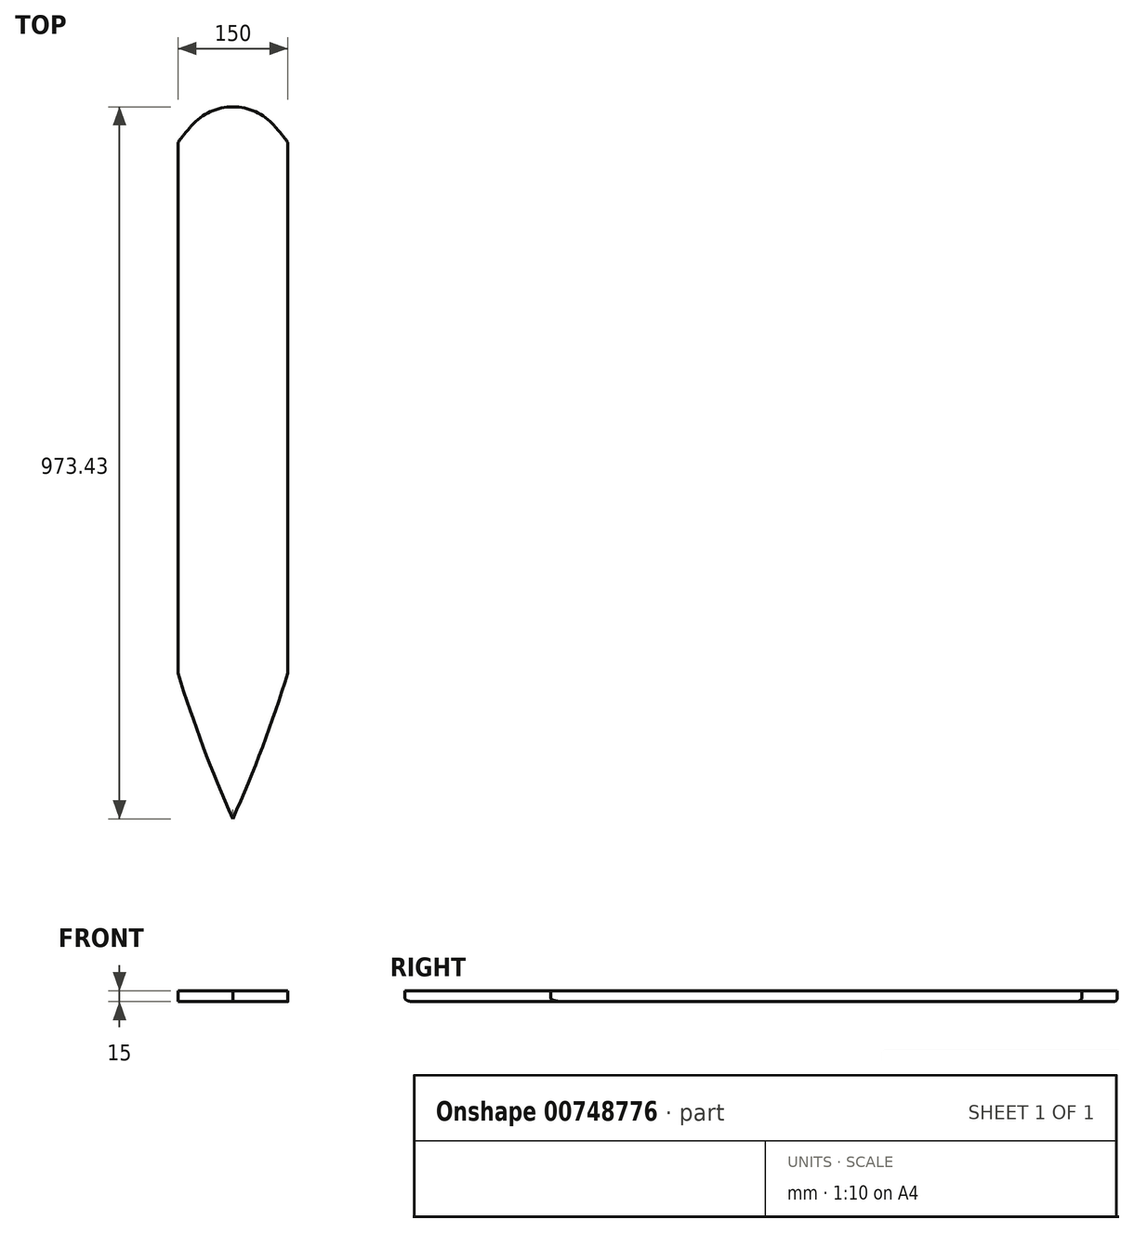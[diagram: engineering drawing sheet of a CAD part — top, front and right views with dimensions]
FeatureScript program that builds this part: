
annotation { "Feature Type Name" : "Feature", "Feature Type Description" : "" }
export const myFeature = defineFeature(function(context is Context, id is Id, definition is map)
    precondition{}
    {
        {
            var Q0;
            Q0=qCreatedBy(makeId("Top.planeOp"),FACE);
            var sketch = newSketch(context, id + "F0", { "sketchPlane" : qUnion([Q0])});
            skLineSegment(sketch, "E0.bottom", {"start": v(150, 500) * mm, "end": v(-150, 500) * mm, "construction": true});
            skLineSegment(sketch, "E0.top", {"start": v(150, -500) * mm, "end": v(-150, -500) * mm, "construction": true});
            skLineSegment(sketch, "E0.left", {"start": v(150, 500) * mm, "end": v(150, -500) * mm});
            skLineSegment(sketch, "E0.right", {"start": v(-150, 500) * mm, "end": v(-150, -500) * mm, "construction": true});
            skPoint(sketch, "E0.middle", {"position": v(0, 0) * mm});
            skLineSegment(sketch, "E1", {"start": v(0, 500) * mm, "end": v(0, -500) * mm, "construction": true});
            skPoint(sketch, "E2.orphan", {"position": v(0, 500) * mm});
            skArc(sketch, "E3", {"start": v(0, 500) * mm, "mid": v(-110.41, 367.7) * mm, "end": v(-150, 200) * mm});
            skArc(sketch, "E4.MirrorCS", {"start": v(150, 200) * mm, "mid": v(112.08, -157.95) * mm, "end": v(0, -500) * mm});
            skArc(sketch, "E5.MirrorCS", {"start": v(0, 500) * mm, "mid": v(110.41, 367.7) * mm, "end": v(150, 200) * mm});
            skArc(sketch, "E6.trimOffspring", {"start": v(-150, 200) * mm, "mid": v(-112.08, -157.95) * mm, "end": v(0, -500) * mm});
            skLineSegment(sketch, "E7", {"start": v(0, 200) * mm, "end": v(-1558.33, 200) * mm, "construction": true});
            skLineSegment(sketch, "E8", {"start": v(0, 200) * mm, "end": v(1558.33, 200) * mm, "construction": true});
            skLineSegment(sketch, "E9.bottom", {"start": v(75, -500) * mm, "end": v(-75, -500) * mm});
            skLineSegment(sketch, "E9.top", {"start": v(75, 500) * mm, "end": v(-75, 500) * mm});
            skLineSegment(sketch, "E9.left", {"start": v(75, -500) * mm, "end": v(75, 500) * mm});
            skLineSegment(sketch, "E9.right", {"start": v(-75, -500) * mm, "end": v(-75, 500) * mm});
            skLineSegment(sketch, "E10.bottom", {"start": v(0, 200) * mm, "end": v(0, 200) * mm});
            skLineSegment(sketch, "E10.top", {"start": v(0, 0) * mm, "end": v(0, 0) * mm});
            skLineSegment(sketch, "E10.left", {"start": v(0, 200) * mm, "end": v(0, 0) * mm});
            skLineSegment(sketch, "E10.right", {"start": v(0, 200) * mm, "end": v(0, 0) * mm});
            skSolve(sketch);
        }
        {
            var Q0;
            {var subQ1=sQuery(id+"F0.wireOp",EDGE,"E4.MirrorCS");var subQ8=sQuery(id+"F0.wireOp",EDGE,"E9.left");var subQ10=makeQuery(id+"F0.imprint","INTERSECT",VERTEX,{"derivedFrom":[subQ1,subQ8]});Q0=makeQuery(id+"F0.imprint","IMPRINT",FACE,{"disambiguationData":[TD([[makeQuery(id+"F0.imprint","IMPRINT",EDGE,{"disambiguationData":[TD([[subQ10,-1.0]])],"derivedFrom":subQ8}),1.0]])]});}
            extrude(context, id + "F1", {"entities" : qUnion([Q0]), "depth" : 15 * mm, "offsetDistance" : 25 * mm});
        }
        {
            var Q0;
            Q0=makeQuery(id+"F1.opExtrude","SWEPT_EDGE",EDGE,{"disambiguationData":[OSD([sQuery(id+"F0.wireOp",EDGE,"E3"),sQuery(id+"F0.wireOp",EDGE,"E5.MirrorCS"),sQuery(id+"F0.wireOp",EDGE,"E9.top")])]});
            fillet(context, id + "F2", {"entities" : qUnion([Q0]), "radius" : 75 * mm, "tangentPropagation" : true, "allowEdgeOverflow" : false});
        }
        {
            var Q0;
            {var subQ0=sQuery(id+"F0.wireOp",EDGE,"E5.MirrorCS");var subQ1=sQuery(id+"F0.wireOp",EDGE,"E3");Q0=makeQuery(id+"F2.opFillet","BLEND_EDGE",EDGE,{"blendedFrom":[makeQuery(id+"F1.opExtrude","SWEPT_EDGE",EDGE,{"disambiguationData":[OSD([subQ1,subQ0,sQuery(id+"F0.wireOp",EDGE,"E9.top")])]}),makeQuery(id+"F1.opExtrude","CAP_FACE",FACE,{"disambiguationData":[OSD([subQ1,sQuery(id+"F0.wireOp",EDGE,"E4.MirrorCS"),subQ0,sQuery(id+"F0.wireOp",EDGE,"E6.trimOffspring"),sQuery(id+"F0.wireOp",EDGE,"E9.left"),sQuery(id+"F0.wireOp",EDGE,"E9.right")])],"isStart":true})],"blendedInto":[makeQuery(id+"F1.opExtrude","CAP_FACE",FACE,{"disambiguationData":[OSD([subQ1,sQuery(id+"F0.wireOp",EDGE,"E4.MirrorCS"),subQ0,sQuery(id+"F0.wireOp",EDGE,"E6.trimOffspring"),sQuery(id+"F0.wireOp",EDGE,"E9.left"),sQuery(id+"F0.wireOp",EDGE,"E9.right")])],"isStart":true})]});}
            fillet(context, id + "F3", {"entities" : qUnion([Q0]), "radius" : 5 * mm, "tangentPropagation" : true, "allowEdgeOverflow" : false});
        }
        {
            var Q0;
            Q0=makeQuery(id+"F1.opExtrude","CAP_EDGE",EDGE,{"disambiguationData":[OSD([sQuery(id+"F0.wireOp",EDGE,"E6.trimOffspring")])],"isStart":true});
            var Q1;
            Q1=makeQuery(id+"F1.opExtrude","CAP_EDGE",EDGE,{"disambiguationData":[OSD([sQuery(id+"F0.wireOp",EDGE,"E4.MirrorCS")])],"isStart":true});
            fillet(context, id + "F4", {"entities" : qUnion([Q0, Q1]), "radius" : 5 * mm, "tangentPropagation" : true, "allowEdgeOverflow" : false});
        }
    });
